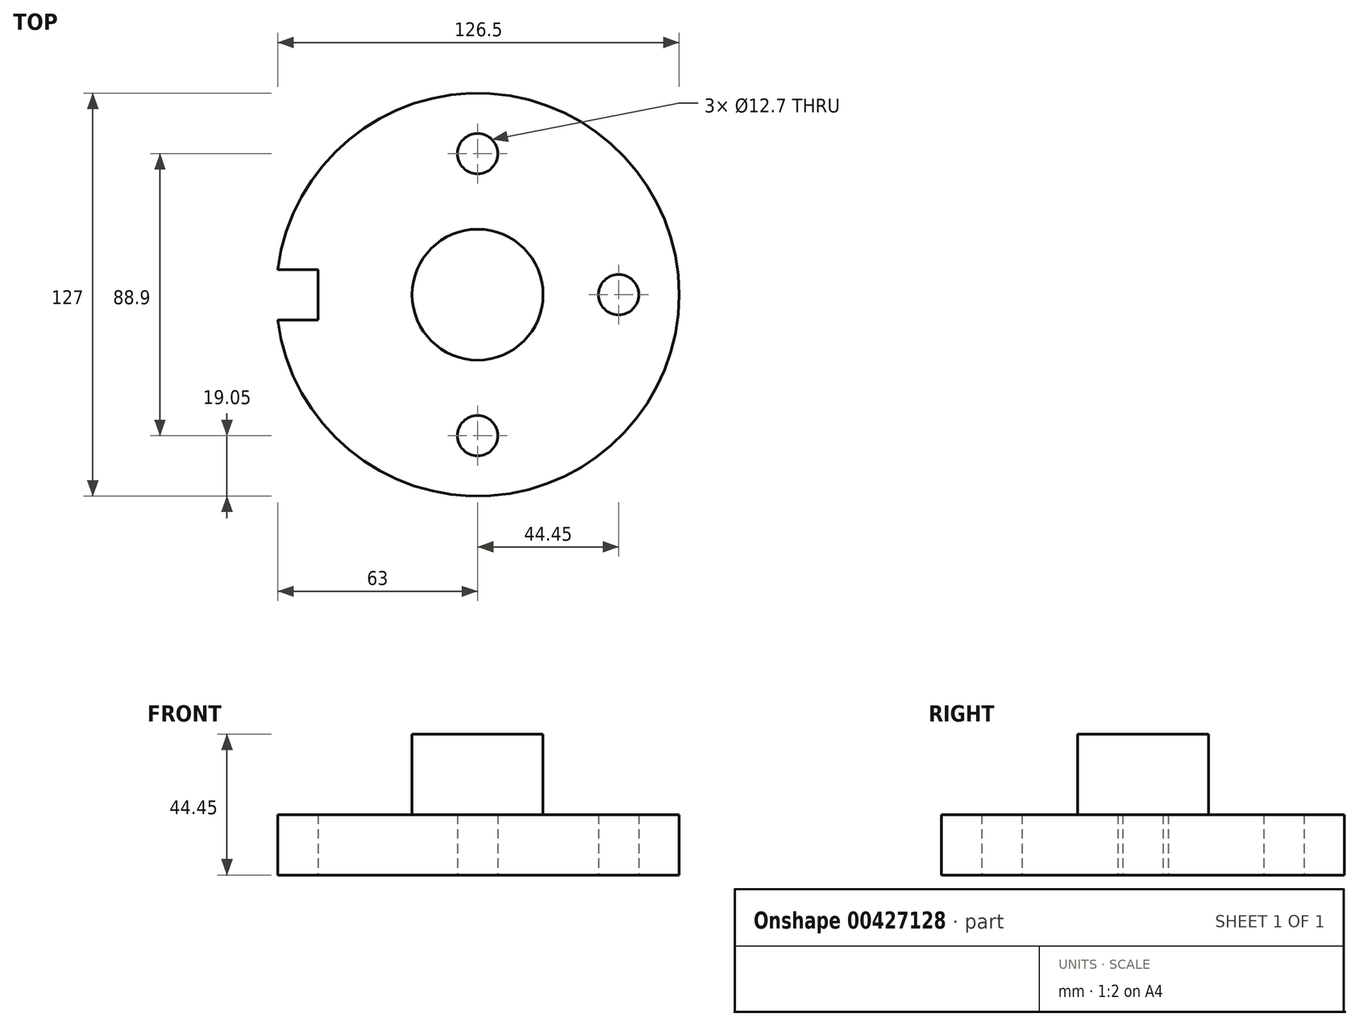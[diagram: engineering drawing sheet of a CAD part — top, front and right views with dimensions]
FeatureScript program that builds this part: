
annotation { "Feature Type Name" : "Feature", "Feature Type Description" : "" }
export const myFeature = defineFeature(function(context is Context, id is Id, definition is map)
    precondition{}
    {
        {
            var Q0;
            Q0=qCreatedBy(makeId("Top.planeOp"),FACE);
            var sketch = newSketch(context, id + "F0", { "sketchPlane" : qUnion([Q0])});
            skArc(sketch, "E0", {"start": v(-63, -7.94) * mm, "mid": v(63.5, 0) * mm, "end": v(-63, 7.94) * mm});
            skCircle(sketch, "E1", {"center": v(44.45, 0) * mm, "radius": 6.35 * mm});
            skCircle(sketch, "E2.1.0", {"center": v(0, 44.45) * mm, "radius": 6.35 * mm});
            skCircle(sketch, "E2.3.0", {"center": v(0, -44.45) * mm, "radius": 6.35 * mm});
            skLineSegment(sketch, "E3.bottom", {"start": v(-63, 7.94) * mm, "end": v(-50.3, 7.94) * mm});
            skLineSegment(sketch, "E3.top", {"start": v(-63, -7.94) * mm, "end": v(-50.3, -7.94) * mm});
            skLineSegment(sketch, "E3.right", {"start": v(-50.3, 7.94) * mm, "end": v(-50.3, -7.94) * mm});
            skSolve(sketch);
        }
        {
            var Q0;
            Q0 = qSketchRegion(id + "F0", true);
            extrude(context, id + "F1", {"entities" : qUnion([Q0]), "depth" : 19.05 * mm});
        }
        {
            var Q0;
            Q0=makeQuery(id+"F1.opExtrude","CAP_FACE",FACE,{"disambiguationData":[OSD([sQuery(id+"F0.wireOp",EDGE,"E0"),sQuery(id+"F0.wireOp",EDGE,"E1"),sQuery(id+"F0.wireOp",EDGE,"E2.1.0"),sQuery(id+"F0.wireOp",EDGE,"E2.3.0"),sQuery(id+"F0.wireOp",EDGE,"E3.bottom"),sQuery(id+"F0.wireOp",EDGE,"E3.top"),sQuery(id+"F0.wireOp",EDGE,"E3.right")])],"isStart":false});
            var sketch = newSketch(context, id + "F2", { "sketchPlane" : qUnion([Q0])});
            skCircle(sketch, "E4", {"center": v(0, 0) * mm, "radius": 20.64 * mm});
            skSolve(sketch);
        }
        {
            var Q0;
            Q0=makeQuery(id+"F2.imprint","IMPRINT",FACE,{"disambiguationData":[TD([[makeQuery(id+"F2.imprint","IMPRINT",EDGE,{"derivedFrom":sQuery(id+"F2.wireOp",EDGE,"E4")}),1.0]])]});
            extrude(context, id + "F3", {"entities" : qUnion([Q0]), "operationType" : NewBodyOperationType.ADD, "depth" : 25.4 * mm});
        }
    });
